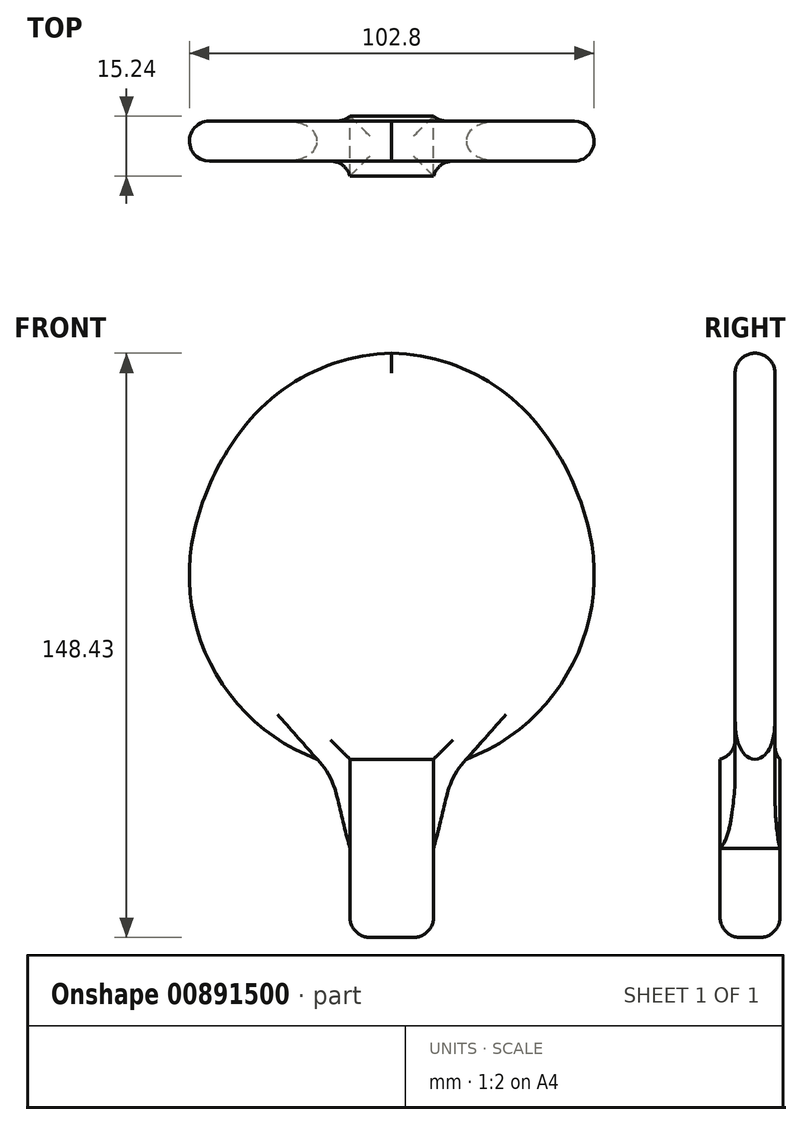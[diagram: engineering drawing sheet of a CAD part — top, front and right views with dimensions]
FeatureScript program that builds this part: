
annotation { "Feature Type Name" : "Feature", "Feature Type Description" : "" }
export const myFeature = defineFeature(function(context is Context, id is Id, definition is map)
    precondition{}
    {
        {
            var Q0;
            Q0=qCreatedBy(makeId("Front.planeOp"),FACE);
            var sketch = newSketch(context, id + "F0", { "sketchPlane" : qUnion([Q0])});
            skLineSegment(sketch, "E0", {"start": v(0, -45.25) * mm, "end": v(-10.62, -45.25) * mm});
            skLineSegment(sketch, "E1", {"start": v(-10.62, -45.25) * mm, "end": v(-10.62, -22.62) * mm});
            skLineSegment(sketch, "E2", {"start": v(0, -45.25) * mm, "end": v(0, 82.2) * mm, "construction": true});
            skFitSpline(sketch, "E3", {"points": [v(-10.62, -22.62) * mm, v(-12.6, -14.81) * mm, v(-15.48, -4.9) * mm, v(-18.95, 0) * mm], "startDerivative": vector(-5.87, 22.01) * mm, "endDerivative": vector(-12.97, 14.67) * mm});
            skArc(sketch, "E4", {"start": v(-50.23, 57.65) * mm, "mid": v(-45.35, 22.99) * mm, "end": v(-18.95, 0) * mm});
            skArc(sketch, "E5", {"start": v(-37.05, 85) * mm, "mid": v(-45.23, 72.1) * mm, "end": v(-50.23, 57.65) * mm});
            skArc(sketch, "E6", {"start": v(0, 103.18) * mm, "mid": v(-20.53, 98.19) * mm, "end": v(-37.05, 85) * mm});
            skLineSegment(sketch, "E7.MirrorCS", {"start": v(0, -45.25) * mm, "end": v(10.62, -45.25) * mm});
            skLineSegment(sketch, "E8.MirrorCS", {"start": v(10.62, -45.25) * mm, "end": v(10.62, -22.62) * mm});
            skFitSpline(sketch, "E9.MirrorCS", {"points": [v(10.62, -22.62) * mm, v(12.6, -14.81) * mm, v(15.48, -4.9) * mm, v(18.95, 0) * mm], "startDerivative": vector(5.87, 22.01) * mm, "endDerivative": vector(12.97, 14.67) * mm});
            skArc(sketch, "E10.MirrorCS", {"start": v(50.23, 57.65) * mm, "mid": v(45.35, 22.99) * mm, "end": v(18.95, 0) * mm});
            skArc(sketch, "E11.MirrorCS", {"start": v(37.05, 85) * mm, "mid": v(45.23, 72.1) * mm, "end": v(50.23, 57.65) * mm});
            skArc(sketch, "E12.MirrorCS", {"start": v(0, 103.18) * mm, "mid": v(20.53, 98.19) * mm, "end": v(37.05, 85) * mm});
            skPoint(sketch, "E13.orphan", {"position": v(-10.62, 0) * mm});
            skPoint(sketch, "E14.orphan", {"position": v(10.62, 0) * mm});
            skSolve(sketch);
        }
        {
            var Q0;
            Q0 = qSketchRegion(id + "F0", true);
            extrude(context, id + "F1", {"entities" : qUnion([Q0]), "depth" : 10.16 * mm, "offsetDistance" : 25.4 * mm});
        }
        {
            var Q0;
            Q0=makeQuery(id+"F1.opExtrude","CAP_FACE",FACE,{"disambiguationData":[OSD([sQuery(id+"F0.wireOp",EDGE,"E0"),sQuery(id+"F0.wireOp",EDGE,"E1"),sQuery(id+"F0.wireOp",EDGE,"E3"),sQuery(id+"F0.wireOp",EDGE,"E4"),sQuery(id+"F0.wireOp",EDGE,"E5"),sQuery(id+"F0.wireOp",EDGE,"E6"),sQuery(id+"F0.wireOp",EDGE,"E7.MirrorCS"),sQuery(id+"F0.wireOp",EDGE,"E8.MirrorCS"),sQuery(id+"F0.wireOp",EDGE,"E9.MirrorCS"),sQuery(id+"F0.wireOp",EDGE,"E10.MirrorCS"),sQuery(id+"F0.wireOp",EDGE,"E11.MirrorCS"),sQuery(id+"F0.wireOp",EDGE,"E12.MirrorCS")])],"isStart":false});
            var sketch = newSketch(context, id + "F2", { "sketchPlane" : qUnion([Q0])});
            skLineSegment(sketch, "E15", {"start": v(-10.62, -45.25) * mm, "end": v(-10.62, 0) * mm});
            skLineSegment(sketch, "E16", {"start": v(-10.62, 0) * mm, "end": v(10.62, 0) * mm});
            skLineSegment(sketch, "E17", {"start": v(10.62, 0) * mm, "end": v(10.62, -45.25) * mm});
            skSolve(sketch);
        }
        {
            var Q0;
            {var subQ3=sQuery(id+"F2.wireOp",EDGE,"E16");Q0=makeQuery(id+"F2.imprint","IMPRINT",FACE,{"disambiguationData":[TD([[makeQuery(id+"F2.imprint","IMPRINT",EDGE,{"derivedFrom":subQ3}),-1.0]])]});}
            extrude(context, id + "F3", {"entities" : qUnion([Q0]), "operationType" : NewBodyOperationType.ADD, "depth" : 3.8 * mm, "offsetDistance" : 25.4 * mm, "hasSecondDirection" : true, "secondDirectionOppositeDirection" : true, "secondDirectionDepth" : 11.43 * mm});
        }
        {
            var Q0;
            Q0=makeQuery(id+"F3.boolean.opBoolean","INTERSECT",EDGE,{"derivedFrom":[makeQuery(id+"F1.opExtrude","CAP_FACE",FACE,{"disambiguationData":[OSD([sQuery(id+"F0.wireOp",EDGE,"E0"),sQuery(id+"F0.wireOp",EDGE,"E1"),sQuery(id+"F0.wireOp",EDGE,"E3"),sQuery(id+"F0.wireOp",EDGE,"E4"),sQuery(id+"F0.wireOp",EDGE,"E5"),sQuery(id+"F0.wireOp",EDGE,"E6"),sQuery(id+"F0.wireOp",EDGE,"E7.MirrorCS"),sQuery(id+"F0.wireOp",EDGE,"E8.MirrorCS"),sQuery(id+"F0.wireOp",EDGE,"E9.MirrorCS"),sQuery(id+"F0.wireOp",EDGE,"E10.MirrorCS"),sQuery(id+"F0.wireOp",EDGE,"E11.MirrorCS"),sQuery(id+"F0.wireOp",EDGE,"E12.MirrorCS")])],"isStart":false}),makeQuery(id+"F3.opExtrude","SWEPT_FACE",FACE,{"disambiguationData":[OSD([sQuery(id+"F2.wireOp",EDGE,"E15")])]})]});
            var Q1;
            Q1=makeQuery(id+"F3.boolean.opBoolean","INTERSECT",EDGE,{"derivedFrom":[makeQuery(id+"F1.opExtrude","CAP_FACE",FACE,{"disambiguationData":[OSD([sQuery(id+"F0.wireOp",EDGE,"E0"),sQuery(id+"F0.wireOp",EDGE,"E1"),sQuery(id+"F0.wireOp",EDGE,"E3"),sQuery(id+"F0.wireOp",EDGE,"E4"),sQuery(id+"F0.wireOp",EDGE,"E5"),sQuery(id+"F0.wireOp",EDGE,"E6"),sQuery(id+"F0.wireOp",EDGE,"E7.MirrorCS"),sQuery(id+"F0.wireOp",EDGE,"E8.MirrorCS"),sQuery(id+"F0.wireOp",EDGE,"E9.MirrorCS"),sQuery(id+"F0.wireOp",EDGE,"E10.MirrorCS"),sQuery(id+"F0.wireOp",EDGE,"E11.MirrorCS"),sQuery(id+"F0.wireOp",EDGE,"E12.MirrorCS")])],"isStart":false}),makeQuery(id+"F3.opExtrude","SWEPT_FACE",FACE,{"disambiguationData":[OSD([sQuery(id+"F2.wireOp",EDGE,"E17")])]})]});
            var Q2;
            Q2=makeQuery(id+"F3.boolean.opBoolean","INTERSECT",EDGE,{"derivedFrom":[makeQuery(id+"F1.opExtrude","CAP_FACE",FACE,{"disambiguationData":[OSD([sQuery(id+"F0.wireOp",EDGE,"E0"),sQuery(id+"F0.wireOp",EDGE,"E1"),sQuery(id+"F0.wireOp",EDGE,"E3"),sQuery(id+"F0.wireOp",EDGE,"E4"),sQuery(id+"F0.wireOp",EDGE,"E5"),sQuery(id+"F0.wireOp",EDGE,"E6"),sQuery(id+"F0.wireOp",EDGE,"E7.MirrorCS"),sQuery(id+"F0.wireOp",EDGE,"E8.MirrorCS"),sQuery(id+"F0.wireOp",EDGE,"E9.MirrorCS"),sQuery(id+"F0.wireOp",EDGE,"E10.MirrorCS"),sQuery(id+"F0.wireOp",EDGE,"E11.MirrorCS"),sQuery(id+"F0.wireOp",EDGE,"E12.MirrorCS")])],"isStart":false}),makeQuery(id+"F3.opExtrude","SWEPT_FACE",FACE,{"disambiguationData":[OSD([sQuery(id+"F2.wireOp",EDGE,"E16")])]})]});
            var Q3;
            Q3=makeQuery(id+"F3.boolean.opBoolean","INTERSECT",EDGE,{"derivedFrom":[makeQuery(id+"F1.opExtrude","CAP_FACE",FACE,{"disambiguationData":[OSD([sQuery(id+"F0.wireOp",EDGE,"E0"),sQuery(id+"F0.wireOp",EDGE,"E1"),sQuery(id+"F0.wireOp",EDGE,"E3"),sQuery(id+"F0.wireOp",EDGE,"E4"),sQuery(id+"F0.wireOp",EDGE,"E5"),sQuery(id+"F0.wireOp",EDGE,"E6"),sQuery(id+"F0.wireOp",EDGE,"E7.MirrorCS"),sQuery(id+"F0.wireOp",EDGE,"E8.MirrorCS"),sQuery(id+"F0.wireOp",EDGE,"E9.MirrorCS"),sQuery(id+"F0.wireOp",EDGE,"E10.MirrorCS"),sQuery(id+"F0.wireOp",EDGE,"E11.MirrorCS"),sQuery(id+"F0.wireOp",EDGE,"E12.MirrorCS")])],"isStart":true}),makeQuery(id+"F3.opExtrude","SWEPT_FACE",FACE,{"disambiguationData":[OSD([sQuery(id+"F2.wireOp",EDGE,"E16")])]})]});
            var Q4;
            Q4=makeQuery(id+"F3.boolean.opBoolean","INTERSECT",EDGE,{"derivedFrom":[makeQuery(id+"F1.opExtrude","CAP_FACE",FACE,{"disambiguationData":[OSD([sQuery(id+"F0.wireOp",EDGE,"E0"),sQuery(id+"F0.wireOp",EDGE,"E1"),sQuery(id+"F0.wireOp",EDGE,"E3"),sQuery(id+"F0.wireOp",EDGE,"E4"),sQuery(id+"F0.wireOp",EDGE,"E5"),sQuery(id+"F0.wireOp",EDGE,"E6"),sQuery(id+"F0.wireOp",EDGE,"E7.MirrorCS"),sQuery(id+"F0.wireOp",EDGE,"E8.MirrorCS"),sQuery(id+"F0.wireOp",EDGE,"E9.MirrorCS"),sQuery(id+"F0.wireOp",EDGE,"E10.MirrorCS"),sQuery(id+"F0.wireOp",EDGE,"E11.MirrorCS"),sQuery(id+"F0.wireOp",EDGE,"E12.MirrorCS")])],"isStart":true}),makeQuery(id+"F3.opExtrude","SWEPT_FACE",FACE,{"disambiguationData":[OSD([sQuery(id+"F2.wireOp",EDGE,"E15")])]})]});
            var Q5;
            Q5=makeQuery(id+"F3.boolean.opBoolean","INTERSECT",EDGE,{"derivedFrom":[makeQuery(id+"F1.opExtrude","CAP_FACE",FACE,{"disambiguationData":[OSD([sQuery(id+"F0.wireOp",EDGE,"E0"),sQuery(id+"F0.wireOp",EDGE,"E1"),sQuery(id+"F0.wireOp",EDGE,"E3"),sQuery(id+"F0.wireOp",EDGE,"E4"),sQuery(id+"F0.wireOp",EDGE,"E5"),sQuery(id+"F0.wireOp",EDGE,"E6"),sQuery(id+"F0.wireOp",EDGE,"E7.MirrorCS"),sQuery(id+"F0.wireOp",EDGE,"E8.MirrorCS"),sQuery(id+"F0.wireOp",EDGE,"E9.MirrorCS"),sQuery(id+"F0.wireOp",EDGE,"E10.MirrorCS"),sQuery(id+"F0.wireOp",EDGE,"E11.MirrorCS"),sQuery(id+"F0.wireOp",EDGE,"E12.MirrorCS")])],"isStart":true}),makeQuery(id+"F3.opExtrude","SWEPT_FACE",FACE,{"disambiguationData":[OSD([sQuery(id+"F2.wireOp",EDGE,"E17")])]})]});
            var Q6;
            {var subQ0=sQuery(id+"F0.wireOp",EDGE,"E7.MirrorCS");var subQ1=sQuery(id+"F0.wireOp",EDGE,"E0");Q6=makeQuery(id+"F3.boolean.opBoolean","MERGE",FACE,{"derivedFrom":[makeQuery(id+"F1.opExtrude","SWEPT_FACE",FACE,{"disambiguationData":[OSD([subQ1,subQ0])]}),makeQuery(id+"F3.opExtrude","SWEPT_FACE",FACE,{"disambiguationData":[OSD([subQ1,subQ0])]})]});}
            var Q7;
            Q7=makeQuery(id+"F1.opExtrude","CAP_EDGE",EDGE,{"disambiguationData":[OSD([sQuery(id+"F0.wireOp",EDGE,"E5")])],"isStart":true});
            var Q8;
            Q8=makeQuery(id+"F1.opExtrude","CAP_EDGE",EDGE,{"disambiguationData":[OSD([sQuery(id+"F0.wireOp",EDGE,"E12.MirrorCS")])],"isStart":true});
            var Q9;
            Q9=makeQuery(id+"F1.opExtrude","CAP_EDGE",EDGE,{"disambiguationData":[OSD([sQuery(id+"F0.wireOp",EDGE,"E4")])],"isStart":false});
            var Q10;
            Q10=makeQuery(id+"F1.opExtrude","CAP_EDGE",EDGE,{"disambiguationData":[OSD([sQuery(id+"F0.wireOp",EDGE,"E11.MirrorCS")])],"isStart":false});
            fillet(context, id + "F4", {"entities" : qUnion([Q0, Q1, Q2, Q3, Q4, Q5, Q6, Q7, Q8, Q9, Q10]), "radius" : 5.08 * mm, "tangentPropagation" : true, "allowEdgeOverflow" : false});
        }
    });
